# Revit family: Контейнер для шприца индивидуальный
name_source: partatom
category: Оборудование
revit_build: Autodesk Revit 2017 (Build: 20170118_1100(x64)
units: mm (PartAtom-declared; Revit-internal decimal feet)

## family parameters
Всегда вертикально = Да
На основе рабочей плоскости = Нет
Общий = Нет
При загрузке вырезать с полостями = Нет
Размер круглого соединителя = Использовать диаметр
Тип детали = Нормальный
Точка расчета площади = Нет

## types (7) — shared parameters
Общ_Единицы измерения = шт.

## per-type parameters (varying)
| type | Общ_Высота | Общ_Глубина | Общ_Масса | Общ_Наименование | Общ_Позиция | Общ_Поставщик | Общ_Тип, марка | Общ_Ширина |
| Амплитуда 2 мл | 26.5 мм | 26.5 мм | 0.19 | Контейнер защитный для шприца, вольфрам 4мм | 65 | Comecer | PST Series | 58 мм |
| Амплитуда 5 мл | 30.5 мм | 30.5 мм | 0.27 | Контейнер защитный для шприца 5 мл, свинцовый эквивалент 5 мм |  | Амплитуда | КС-204А | 66 мм |
| Амплитуда 10 мл | 33 мм | 33 мм | 0.360 | Контейнер защитный для шприца 10 мл, свинцовый эквивалент 5 мм |  | Амплитуда | КС-205А | 78.5 мм |
| Comecer BHP 1 мл | 23 мм | 23 мм |  | Контейнер защитный для шприца 1 мл, защита из 7,5 мм вольфрама |  | Comecer | BHP | 72 мм |
| Comecer BHP 2/3 мл | 27 мм | 27 мм |  | Контейнер защитный для шприца 2/3 мл, защита из 7,5 мм вольфрама |  | Comecer | BHP | 73 мм |
| Comecer BHP 5 мл | 31 мм | 31 мм |  | Контейнер защитный для шприца 5 мл, защита из 7,5 мм вольфрама |  | Comecer | BHP | 60 мм |
| Comecer BHP 10 мл | 33 мм | 33 мм |  | Контейнер защитный для шприца 10 мл, защита из 7,5 мм вольфрама |  | Comecer | BHP | 75 мм |
